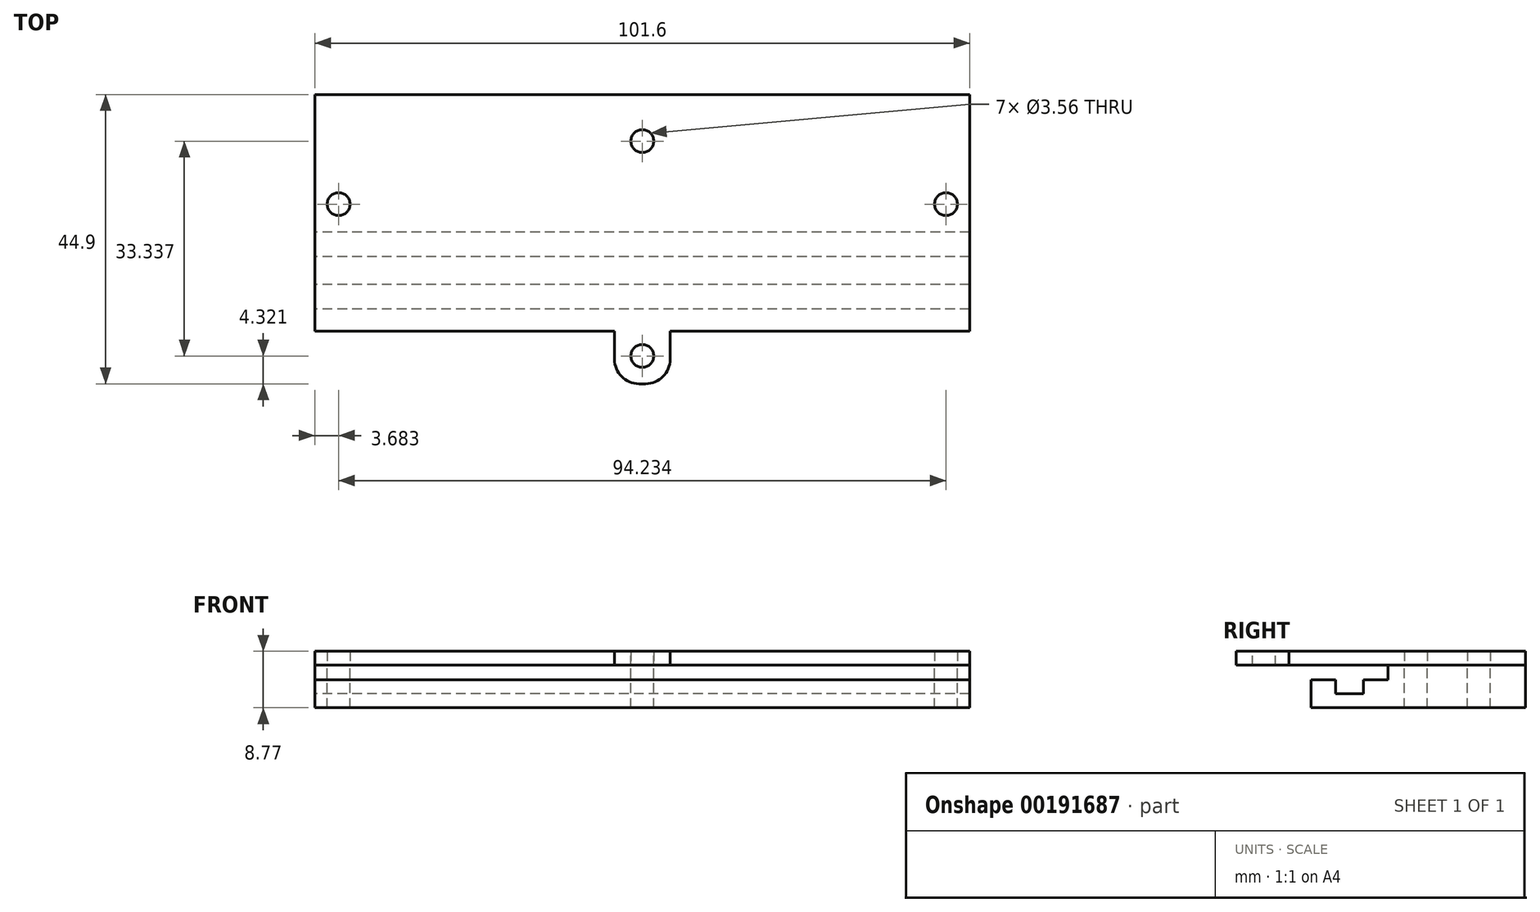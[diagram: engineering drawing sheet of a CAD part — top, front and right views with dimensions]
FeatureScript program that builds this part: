
annotation { "Feature Type Name" : "Feature", "Feature Type Description" : "" }
export const myFeature = defineFeature(function(context is Context, id is Id, definition is map)
    precondition{}
    {
        {
            var Q0;
            Q0=qCreatedBy(makeId("Right.planeOp"),FACE);
            var sketch = newSketch(context, id + "F0", { "sketchPlane" : qUnion([Q0])});
            skLineSegment(sketch, "E0.top", {"start": v(-6.45, -4.32) * mm, "end": v(26.83, -4.32) * mm});
            skLineSegment(sketch, "E0.left", {"start": v(-6.45, 0) * mm, "end": v(-6.45, -4.32) * mm});
            skLineSegment(sketch, "E0.right", {"start": v(26.83, 0) * mm, "end": v(26.83, -4.32) * mm});
            skLineSegment(sketch, "E1", {"start": v(-2.64, 0) * mm, "end": v(-2.64, -2.16) * mm});
            skLineSegment(sketch, "E2", {"start": v(-2.64, -2.16) * mm, "end": v(1.68, -2.16) * mm});
            skLineSegment(sketch, "E3", {"start": v(1.68, -2.16) * mm, "end": v(1.68, 0) * mm});
            skLineSegment(sketch, "E4", {"start": v(-6.45, 0) * mm, "end": v(-2.64, 0) * mm});
            skLineSegment(sketch, "E5", {"start": v(1.68, 0) * mm, "end": v(5.5, 0) * mm});
            skLineSegment(sketch, "E6", {"start": v(26.83, 0) * mm, "end": v(26.83, 2.29) * mm});
            skLineSegment(sketch, "E7", {"start": v(26.83, 2.29) * mm, "end": v(5.5, 2.29) * mm});
            skLineSegment(sketch, "E8", {"start": v(5.5, 2.29) * mm, "end": v(5.5, 0) * mm});
            skSolve(sketch);
        }
        {
            var Q0;
            Q0=makeQuery(id+"F0.imprint","IMPRINT",FACE,{"disambiguationData":[TD([[makeQuery(id+"F0.imprint","IMPRINT",EDGE,{"derivedFrom":sQuery(id+"F0.wireOp",EDGE,"E0.top")}),1.0]])]});
            extrude(context, id + "F1", {"entities" : qUnion([Q0]), "depth" : 101.6 * mm});
        }
        {
            var Q0;
            Q0=makeQuery(id+"F1.opExtrude","SWEPT_FACE",FACE,{"disambiguationData":[OSD([sQuery(id+"F0.wireOp",EDGE,"E7")])]});
            var sketch = newSketch(context, id + "F2", { "sketchPlane" : qUnion([Q0])});
            skCircle(sketch, "E9", {"center": v(97.92, 9.8) * mm, "radius": 1.78 * mm});
            skCircle(sketch, "E10", {"center": v(97.92, 22.5) * mm, "radius": 1.78 * mm, "construction": true});
            skCircle(sketch, "E11", {"center": v(3.68, 9.8) * mm, "radius": 1.78 * mm});
            skCircle(sketch, "E12", {"center": v(3.68, 22.5) * mm, "radius": 1.78 * mm, "construction": true});
            skCircle(sketch, "E13", {"center": v(50.8, 9.8) * mm, "radius": 1.78 * mm, "construction": true});
            skPoint(sketch, "E13.centerSnap0", {"position": v(50.8, 5.5) * mm});
            skCircle(sketch, "E14", {"center": v(50.8, 19.59) * mm, "radius": 1.78 * mm});
            skSolve(sketch);
        }
        {
            var Q0;
            Q0=qSketchRegion(id+"F2",true);
            extrude(context, id + "F3", {"entities" : qUnion([Q0]), "operationType" : NewBodyOperationType.REMOVE, "endBound" : BoundingType.THROUGH_ALL, "oppositeDirection" : true, "depth" : 25.4 * mm});
        }
        {
            var Q0;
            Q0=qCreatedBy(makeId("Right.planeOp"),FACE);
            var sketch = newSketch(context, id + "F4", { "sketchPlane" : qUnion([Q0])});
            skLineSegment(sketch, "E15", {"start": v(-9.88, 2.29) * mm, "end": v(-9.88, 4.45) * mm});
            skLineSegment(sketch, "E16.0", {"start": v(26.83, 2.29) * mm, "end": v(5.5, 2.29) * mm});
            skLineSegment(sketch, "E17", {"start": v(-9.88, 2.29) * mm, "end": v(26.83, 2.29) * mm});
            skLineSegment(sketch, "E18", {"start": v(26.83, 4.45) * mm, "end": v(26.83, 2.29) * mm});
            skLineSegment(sketch, "E19", {"start": v(26.83, 4.45) * mm, "end": v(-9.88, 4.45) * mm});
            skSolve(sketch);
        }
        {
            var Q0;
            {var subQ0=sQuery(id+"F4.wireOp",EDGE,"E15");Q0=makeQuery(id+"F4.imprint","IMPRINT",FACE,{"disambiguationData":[TD([[makeQuery(id+"F4.imprint","IMPRINT",EDGE,{"derivedFrom":subQ0}),-1.0]])]});}
            var Q1;
            Q1=makeQuery(id+"F1.opExtrude","CAP_FACE",FACE,{"disambiguationData":[OSD([sQuery(id+"F0.wireOp",EDGE,"E0.top"),sQuery(id+"F0.wireOp",EDGE,"E0.left"),sQuery(id+"F0.wireOp",EDGE,"E0.right"),sQuery(id+"F0.wireOp",EDGE,"E1"),sQuery(id+"F0.wireOp",EDGE,"E2"),sQuery(id+"F0.wireOp",EDGE,"E3"),sQuery(id+"F0.wireOp",EDGE,"E4"),sQuery(id+"F0.wireOp",EDGE,"E5"),sQuery(id+"F0.wireOp",EDGE,"E6"),sQuery(id+"F0.wireOp",EDGE,"E7"),sQuery(id+"F0.wireOp",EDGE,"E8")])],"isStart":false});
            extrude(context, id + "F5", {"entities" : qUnion([Q0]), "endBound" : BoundingType.UP_TO_SURFACE, "endBoundEntityFace" : qUnion([Q1]), "depth" : 25.4 * mm});
        }
        {
            var Q0;
            Q0=makeQuery(id+"F5.opExtrude","SWEPT_FACE",FACE,{"disambiguationData":[OSD([sQuery(id+"F4.wireOp",EDGE,"E17")])]});
            var sketch = newSketch(context, id + "F6", { "sketchPlane" : qUnion([Q0])});
            skCircle(sketch, "E20.0", {"center": v(97.92, -9.8) * mm, "radius": 1.78 * mm});
            skCircle(sketch, "E20.1", {"center": v(50.8, -9.8) * mm, "radius": 1.78 * mm, "construction": true});
            skCircle(sketch, "E20.2", {"center": v(3.68, -9.8) * mm, "radius": 1.78 * mm});
            skCircle(sketch, "E20.3", {"center": v(3.68, -22.5) * mm, "radius": 1.78 * mm, "construction": true});
            skCircle(sketch, "E20.4", {"center": v(50.8, -19.59) * mm, "radius": 1.78 * mm});
            skCircle(sketch, "E20.5", {"center": v(97.92, -22.5) * mm, "radius": 1.78 * mm, "construction": true});
            skSolve(sketch);
        }
        {
            var Q0;
            Q0=qSketchRegion(id+"F6",true);
            extrude(context, id + "F7", {"entities" : qUnion([Q0]), "operationType" : NewBodyOperationType.REMOVE, "endBound" : BoundingType.THROUGH_ALL, "oppositeDirection" : true, "depth" : 25.4 * mm});
        }
        {
            var Q0;
            Q0=makeQuery(id+"F5.opExtrude","SWEPT_FACE",FACE,{"disambiguationData":[OSD([sQuery(id+"F4.wireOp",EDGE,"E19")])]});
            var sketch = newSketch(context, id + "F8", { "sketchPlane" : qUnion([Q0])});
            skLineSegment(sketch, "E21.bottom", {"start": v(46.48, -9.88) * mm, "end": v(55.12, -9.88) * mm});
            skLineSegment(sketch, "E21.top", {"start": v(46.48, -18.07) * mm, "end": v(55.12, -18.07) * mm});
            skLineSegment(sketch, "E21.left", {"start": v(46.48, -9.88) * mm, "end": v(46.48, -18.07) * mm});
            skLineSegment(sketch, "E21.right", {"start": v(55.12, -9.88) * mm, "end": v(55.12, -18.07) * mm});
            skPoint(sketch, "E22", {"position": v(50.8, -18.07) * mm});
            skCircle(sketch, "E23", {"center": v(50.8, -13.75) * mm, "radius": 1.78 * mm});
            skSolve(sketch);
        }
        {
            var Q0;
            Q0 = qSketchRegion(id + "F8", true);
            var Q1;
            Q1=makeQuery(id+"F5.opExtrude","SWEPT_FACE",FACE,{"disambiguationData":[OSD([sQuery(id+"F4.wireOp",EDGE,"E17")])]});
            extrude(context, id + "F9", {"entities" : qUnion([Q0]), "operationType" : NewBodyOperationType.ADD, "endBound" : BoundingType.UP_TO_SURFACE, "oppositeDirection" : true, "endBoundEntityFace" : qUnion([Q1]), "depth" : 25.4 * mm});
        }
        {
            var Q0;
            Q0=makeQuery(id+"F9.opExtrude","SWEPT_EDGE",EDGE,{"disambiguationData":[OSD([sQuery(id+"F8.wireOp",EDGE,"E21.top"),sQuery(id+"F8.wireOp",EDGE,"E21.right")])]});
            var Q1;
            Q1=makeQuery(id+"F9.opExtrude","SWEPT_EDGE",EDGE,{"disambiguationData":[OSD([sQuery(id+"F8.wireOp",EDGE,"E21.top"),sQuery(id+"F8.wireOp",EDGE,"E21.left")])]});
            fillet(context, id + "F10", {"entities" : qUnion([Q0, Q1]), "radius" : 3.8 * mm, "tangentPropagation" : true, "allowEdgeOverflow" : false});
        }
    });
